# Revit family: IS_Connect_Multiproduct_BIM_DE_E7856;E7861
name_source: partatom
category: Plumbing Fixtures
revit_build: Autodesk Revit MEP 2016 (Build: 20161004_0715(x64)
units: mm (PartAtom-declared; Revit-internal decimal feet)

## family parameters
Cut with Voids When Loaded = No
Host = Face
OmniClass Number = 23.45.05.21.11.11
OmniClass Title = Water Operated Water Closets
Part Type = Normal
Room Calculation Point = No
Round Connector Dimension = Use Diameter
Shared = Yes

## types (4) — shared parameters
Accessories = www.idealstandard.de\ersatzteile
AreaUnits = millimeters
Assembly Code = C1030200
AssetType = Fixed
CodePerformance = DIN EN 997, CL1-6-VRII, DIN EN 33
Color = White
ConnectionType = Plumbing
CurrencyUnit = €
DurationUnit = year
ExpectedLife = 25
Features = CONNECT ARC cistern 360x175mm
Finish = White
IfcExportAs = IfcSanitaryType
IfcExportType = WCCISTERNS
InstallationDate = 1900-12-31T23:59:59
InstallationInstructions = www.idealstandard.de\produkte
LinearUnits = millimeters
ManufacturerURL = www.idealstandard.de
Material = Vitreous china
NominalHeight = 376 mm
NominalLength = 177 mm
NominalWidth = 362 mm
ProductInformation = www.idealstandard.de
Shape = Sculptured
Size = 376 x 361 x 176 mm
Space = Internal
URL = www.idealstandard.de
Uniclass2015Code = Pr_40_20_93_89
Uniclass2015Title = WC cisterns
Uniclass2015Version = Products v1.1
Version = 1
VolumeUnits = Litres
zero-valued in all types: CWFU, Cost, Default Elevation, HWFU, NominalDepth, WFU

## per-type parameters (varying)
| type | BIMObjectName | BarCode | GrossWeight | Model | ModelNumber | ModelReference | Name |
| E786101 - CONNECT ARC CIST SI WHITE 6/3 | ISI_IdealStandard_WCPans_CONNECT_E786101 | 5017830389323 | 12,83 kg | E786101 | E786101 | IS Spülkasten CONNECT ARC, 6 Liter, Zulauf seitlich, 360x176x376mm, Weiß | ISI_IdealStandard_WCPans_CONNECT_E786101 |
| E785601 - CONNECT ARC CIST BI WHITE 6/3 | ISI_IdealStandard_WCPans_CONNECT_E785601 | 5017830390466 | 12,87 kg | E785601 | E785601 | IS Spülkasten CONNECT ARC, 6 Liter, Zulauf unten, 360x176x376mm, Weiß | ISI_IdealStandard_WCPans_CONNECT_E785601 |
| E7856MA - CONNECT ARC cistern 360x175mm | ISI_IdealStandard_WCPans_CONNECT_E7856MA | 5017830398943 | 12,87 kg | E7856MA | E7856MA | IS Spülkasten CONNECT ARC, 6 Liter, Zulauf unten, 360x176x376mm, Weiß m.IP | ISI_IdealStandard_WCPans_CONNECT_E7856MA |
| E7861MA - CONNECT ARC cistern 360x175mm | ISI_IdealStandard_WCPans_CONNECT_E786101 | 5017830396178 | 12,83 kg | E7861MA | E7861MA | IS Spülkasten CONNECT ARC, 6 Liter, Zulauf seitlich, 360x176x376mm, Weiß m.IP | ISI_IdealStandard_WCPans_CONNECT_E7861MA |

## geometry (parser evidence)
native form markers: Blend x4, Sweep x2
no freeform markers — native parametric forms only
